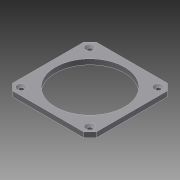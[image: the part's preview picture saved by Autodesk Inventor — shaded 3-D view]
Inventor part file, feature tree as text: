
AUTODESK INVENTOR PART (.ipt)
format: ipt  version: 2022 (Build 260153000, 153)  size: 139,264 bytes
history: native  units: mm
features: other x6, reference x6, sketch x2, extrude x1, hole x1
ambient origin geometry x8: Origin, YZ Plane, XZ Plane, XY Plane, X Axis, Y Axis, Z Axis, Center Point
bodies: Body1 (feature_tree)
feature tree (16):
  other  "Твердое тело1"
  other  "РабПлоскость1"
  extrude  "Выдавливание1"  Depth=4.0mm TaperAngle=0.0deg
  hole  "Отверстие1"  [1 undecoded]
  sketch  "Эскиз1"
  reference  "Ссылка1"
  reference  "Ссылка2"
  sketch  "Эскиз2"
  reference  "Ссылка7"
  reference  "Ссылка8"
  reference  "Ссылка9"
  reference  "Ссылка10"
  parser-record x1  (decoder bookkeeping rows leaked as tree rows — omitted from the tree; the rows remain in map.json)
  other  "Nema17.iam"
  other  "Основание_нижнее:1"
  other  "Корпус:1"
note: 1 required parameter value undecoded (feature->parameter linkage not recoverable at this tier; creation-order binding heuristic only, values carry confidence <= 0.55)
note: 1 file-system path scrubbed to <path> (originals preserved in map.json)
